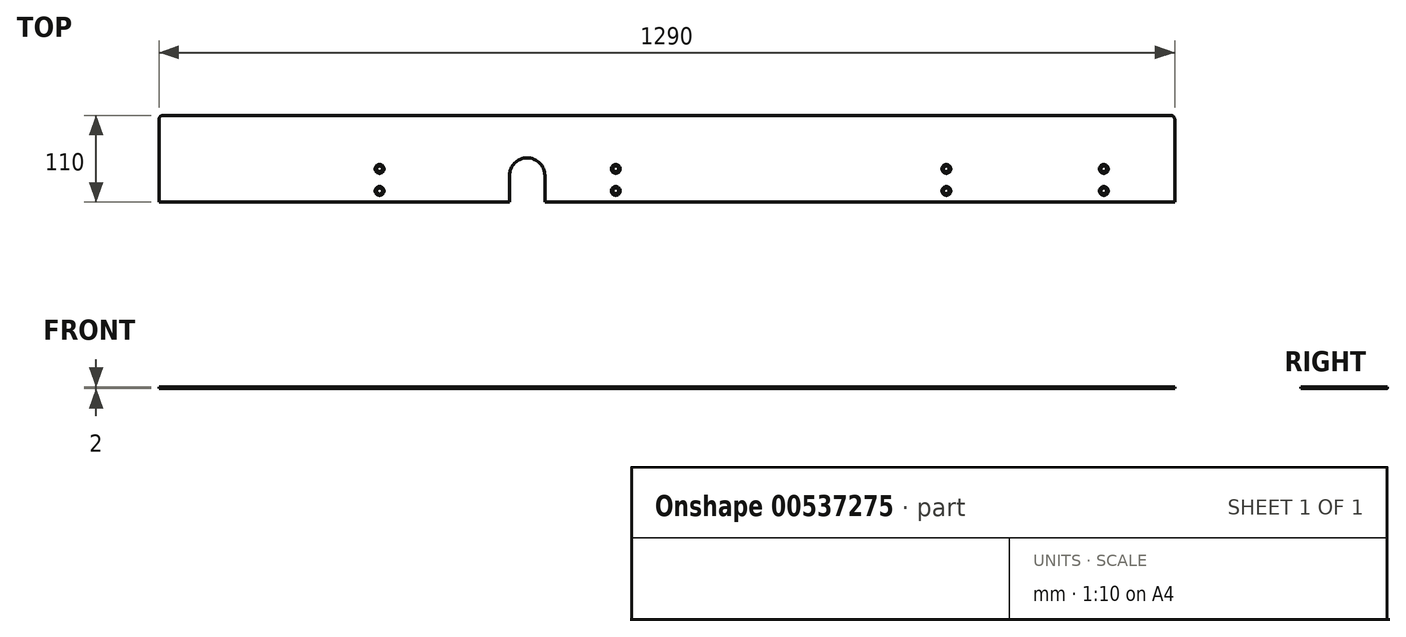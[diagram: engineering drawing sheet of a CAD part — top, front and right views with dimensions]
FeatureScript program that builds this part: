
annotation { "Feature Type Name" : "Feature", "Feature Type Description" : "" }
export const myFeature = defineFeature(function(context is Context, id is Id, definition is map)
    precondition{}
    {
        {
            var Q0;
            Q0=qCreatedBy(makeId("Top.planeOp"),FACE);
            var sketch = newSketch(context, id + "F0", { "sketchPlane" : qUnion([Q0])});
            skLineSegment(sketch, "E0.bottom", {"start": v(0, 0) * mm, "end": v(-1290, 0) * mm});
            skLineSegment(sketch, "E0.top", {"start": v(-5, 110) * mm, "end": v(-1285, 110) * mm});
            skLineSegment(sketch, "E0.left", {"start": v(0, 0) * mm, "end": v(0, 105) * mm});
            skLineSegment(sketch, "E0.right", {"start": v(-1290, 0) * mm, "end": v(-1290, 105) * mm});
            skLineSegment(sketch, "E1.bottom", {"start": v(-845, 0) * mm, "end": v(-800, 0) * mm});
            skLineSegment(sketch, "E1.top", {"start": v(-845, 33.5) * mm, "end": v(-800, 33.5) * mm});
            skLineSegment(sketch, "E1.left", {"start": v(-845, 0) * mm, "end": v(-845, 33.5) * mm});
            skLineSegment(sketch, "E1.right", {"start": v(-800, 0) * mm, "end": v(-800, 33.5) * mm});
            skArc(sketch, "E2", {"start": v(-800, 33.5) * mm, "mid": v(-822.5, 56) * mm, "end": v(-845, 33.5) * mm});
            skPoint(sketch, "E3.visualSharp", {"position": v(-1290, 110) * mm});
            skArc(sketch, "E3.filletArc", {"start": v(-1285, 110) * mm, "mid": v(-1288.54, 108.54) * mm, "end": v(-1290, 105) * mm});
            skPoint(sketch, "E4.visualSharp", {"position": v(0, 110) * mm});
            skArc(sketch, "E4.filletArc", {"start": v(0, 105) * mm, "mid": v(-1.46, 108.54) * mm, "end": v(-5, 110) * mm});
            skLineSegment(sketch, "E5", {"start": v(-1290, 0) * mm, "end": v(-1290, 56) * mm, "construction": true});
            skLineSegment(sketch, "E6", {"start": v(-1290, 56) * mm, "end": v(0, 56) * mm, "construction": true});
            skLineSegment(sketch, "E7", {"start": v(-1290, 28) * mm, "end": v(0, 28) * mm, "construction": true});
            skLineSegment(sketch, "E8", {"start": v(-1290, 14) * mm, "end": v(0, 14) * mm, "construction": true});
            skLineSegment(sketch, "E9", {"start": v(0, 42) * mm, "end": v(-1290, 42) * mm, "construction": true});
            skPoint(sketch, "E10", {"position": v(-1010, 42) * mm});
            skPoint(sketch, "E11", {"position": v(-1010, 14) * mm});
            skPoint(sketch, "E12", {"position": v(-710, 42) * mm});
            skPoint(sketch, "E13", {"position": v(-710, 14) * mm});
            skPoint(sketch, "E14", {"position": v(-290, 42) * mm});
            skPoint(sketch, "E15", {"position": v(-290, 14) * mm});
            skPoint(sketch, "E16", {"position": v(-90, 42) * mm});
            skPoint(sketch, "E17", {"position": v(-90, 14) * mm});
            skSolve(sketch);
        }
        {
            var Q0;
            Q0=makeQuery(id+"F0.imprint","IMPRINT",FACE,{"disambiguationData":[TD([[makeQuery(id+"F0.imprint","IMPRINT",EDGE,{"derivedFrom":sQuery(id+"F0.wireOp",EDGE,"E0.top")}),1.0]])]});
            extrude(context, id + "F1", {"entities" : qUnion([Q0]), "oppositeDirection" : true, "depth" : 2 * mm, "offsetDistance" : 25 * mm});
        }
        {
            var Q0;
            Q0=sQuery(id+"F0.wireOp",VERTEX,"E10");
            var Q1;
            Q1=sQuery(id+"F0.wireOp",VERTEX,"E11");
            var Q2;
            Q2=sQuery(id+"F0.wireOp",VERTEX,"E12");
            var Q3;
            Q3=sQuery(id+"F0.wireOp",VERTEX,"E13");
            var Q4;
            Q4=sQuery(id+"F0.wireOp",VERTEX,"E14");
            var Q5;
            Q5=sQuery(id+"F0.wireOp",VERTEX,"E15");
            var Q6;
            Q6=sQuery(id+"F0.wireOp",VERTEX,"E16");
            var Q7;
            Q7=sQuery(id+"F0.wireOp",VERTEX,"E17");
            var Q8;
            Q8=makeQuery(id+"F1.opExtrude","SWEPT_BODY",BODY,{"disambiguationData":[OSD([sQuery(id+"F0.wireOp",EDGE,"E0.bottom"),sQuery(id+"F0.wireOp",EDGE,"E0.top"),sQuery(id+"F0.wireOp",EDGE,"E0.left"),sQuery(id+"F0.wireOp",EDGE,"E0.right"),sQuery(id+"F0.wireOp",EDGE,"E1.left"),sQuery(id+"F0.wireOp",EDGE,"E1.right"),sQuery(id+"F0.wireOp",EDGE,"E2"),sQuery(id+"F0.wireOp",EDGE,"E3.filletArc"),sQuery(id+"F0.wireOp",EDGE,"E4.filletArc")])]});
            hole(context, id + "F2", {"style" : HoleStyle.C_SINK, "endStyle" : HoleEndStyle.THROUGH, "standardTappedOrClearance" : lookupTablePath({ "standard" : "ISO", "fit" : "Normal", "size" : "M5", "type" : "Clearance" }), "standardBlindInLast" : lookupTablePath({ "fit" : "Standard", "standard" : "ISO", "size" : "M5", "type" : "Clearance" }), "holeDiameter" : 5.5 * mm, "cSinkDiameter" : 11.2 * mm, "cSinkAngle" : 90 * degree, "isTappedThrough" : true, "tappedDepth" : 12 * mm, "tapClearance" : 3, "locations" : qUnion([Q0, Q1, Q2, Q3, Q4, Q5, Q6, Q7]), "scope" : qUnion([Q8])});
        }
    });
